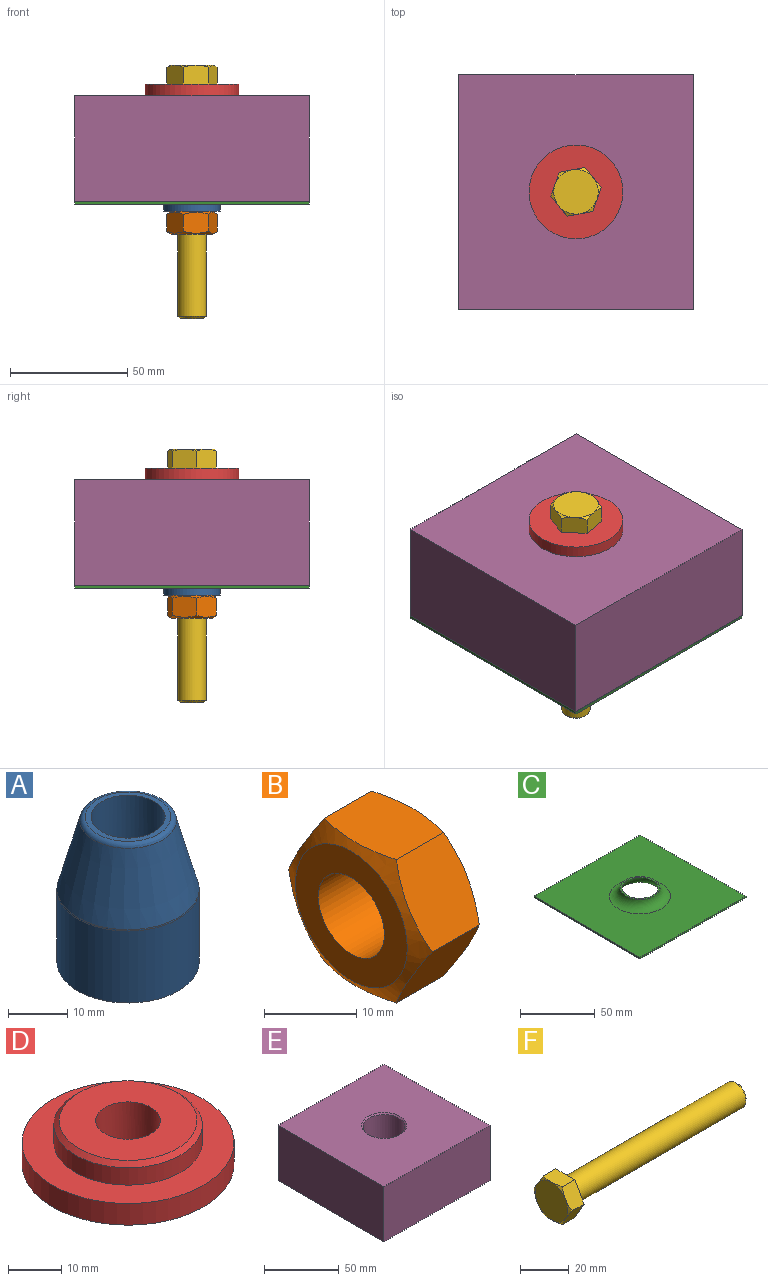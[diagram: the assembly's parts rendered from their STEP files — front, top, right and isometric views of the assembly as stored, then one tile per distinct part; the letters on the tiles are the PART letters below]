
ASSEMBLY  parts=6 mates=10
PART A: 7 faces, bbox 26x26x30 mm
  f0: cylinder r=12mm len=24mm, axis (0,0,-1), area 1121mm2, adj f2,f5
  f1: plane 14.43x14.43mm, normal (0,0,1), area 40.8mm2, adj f3,f6
  f2: plane 24x24mm, normal (0,0,-1), area 329.7mm2, adj f0,f3
  f3: cylinder r=6.25mm len=30mm, axis (0,0,-1), area 1178.1mm2, adj f1,f2
  f4: cone r=7.98mm half-angle=15deg, axis (0,0,-1), area 925.9mm2, adj f5,f6
  f5: torus R=11mm, axis (0,0,1), area 19.7mm2, adj f0,f4
  f6: torus R=7.21mm, axis (0,0,1), area 64mm2, adj f1,f4
PART B: 11 faces, bbox 10x21.9x21.9 mm
  f0: plane 17.1x17.1mm, normal (1,0,0), area 149.4mm2, adj f1,f4
  f1: cone r=11.4mm half-angle=60deg, axis (-1,0,0), area 95.8mm2, adj f0,f5,f6,f7,f8,f9,f10
  f2: cone r=8.55mm half-angle=60deg, axis (1,0,0), area 95.8mm2, adj f3,f5,f6,f7,f8,f9,f10
  f3: plane 17.1x17.1mm, normal (-1,0,0), area 149.4mm2, adj f2,f4
  f4: cylinder r=5.05mm len=10.11mm, axis (1,0,0), area 317.5mm2, adj f0,f3
  f5: plane 10.98x8.91mm, normal (0,0,1), area 91.3mm2, adj f1,f2,f6,f10
  f6: plane 9.5x8.91mm, normal (0,0.87,0.5), area 91.3mm2, adj f1,f2,f5,f7
  f7: plane 9.5x8.91mm, normal (0,0.87,-0.5), area 91.3mm2, adj f1,f2,f6,f8
  f8: plane 10.98x8.91mm, normal (0,0,-1), area 91.3mm2, adj f1,f2,f7,f9
  f9: plane 9.5x8.91mm, normal (0,-0.87,-0.5), area 91.3mm2, adj f1,f2,f8,f10
  f10: plane 9.5x8.91mm, normal (0,-0.87,0.5), area 91.3mm2, adj f1,f2,f5,f9
PART C: 9 faces, bbox 100x100x8.4 mm
  f0: plane 100x1.2mm, normal (0,-1,0), area 120mm2, adj f1,f3,f5,f7
  f1: plane 100x1.2mm, normal (-1,0,0), area 120mm2, adj f0,f2,f5,f7
  f2: plane 100x1.2mm, normal (0,1,0), area 120mm2, adj f1,f3,f5,f7
  f3: plane 100x1.2mm, normal (1,0,0), area 120mm2, adj f0,f2,f5,f7
  f4: plane 26.4x26.4mm, normal (0,0,1), area 95.1mm2, adj f6,f8
  f5: plane 100x100mm, normal (0,0,-1), area 8693.8mm2, adj f0,f1,f2,f3,f6
  f6: torus R=20.39mm, axis (0,0,1), area 1217mm2, adj f4,f5
  f7: plane 100x100mm, normal (0,0,1), area 8693.8mm2, adj f0,f1,f2,f3,f8
  f8: torus R=20.39mm, axis (0,0,1), area 1090.1mm2, adj f4,f7
PART D: 7 faces, bbox 40x40x10 mm
  f0: cylinder r=20mm len=40mm, axis (0,0,-1), area 628.3mm2, adj f1,f2
  f1: plane 40x40mm, normal (0,0,1), area 640.9mm2, adj f0,f3
  f2: plane 40x40mm, normal (0,0,-1), area 1139.7mm2, adj f0,f5
  f3: cylinder r=14mm len=28mm, axis (0,0,-1), area 351.9mm2, adj f1,f6
  f4: plane 26x26mm, normal (0,0,1), area 414mm2, adj f5,f6
  f5: cylinder r=6.1mm len=12.2mm, axis (0,0,-1), area 383.3mm2, adj f2,f4
  f6: cone r=13mm half-angle=45deg, axis (0,0,-1), area 120mm2, adj f3,f4
PART E: 9 faces, bbox 100x100x45 mm
  f0: plane 100x45mm, normal (1,0,0), area 4500mm2, adj f1,f3,f4,f5
  f1: plane 100x45mm, normal (0,1,0), area 4500mm2, adj f0,f2,f4,f5
  f2: plane 100x45mm, normal (-1,0,0), area 4500mm2, adj f1,f3,f4,f5
  f3: plane 100x45mm, normal (0,-1,0), area 4500mm2, adj f0,f2,f4,f5
  f4: plane 100x100mm, normal (0,0,1), area 9293.1mm2, adj f0,f1,f2,f3,f8
  f5: plane 100x100mm, normal (0,0,-1), area 8743.4mm2, adj f0,f1,f2,f3,f7
  f6: cylinder r=14mm len=38mm, axis (0,0,-1), area 3342.7mm2, adj f7,f8
  f7: torus R=20mm, axis (0,0,1), area 958.2mm2, adj f5,f6
  f8: cone r=15mm half-angle=45deg, axis (0,0,1), area 128.8mm2, adj f4,f6
PART F: 18 faces, bbox 108x21.9x21.9 mm
  f0: plane 21.94x19mm, normal (1,0,0), area 158.7mm2, adj f1,f5,f6,f7,f8,f9,f10
  f1: torus R=7mm, axis (1,0,0), area 62.8mm2, adj f0,f4
  f2: plane 9.85x9.85mm, normal (1,0,0), area 76.2mm2, adj f3
  f3: cone r=6mm half-angle=45deg, axis (-1,0,0), area 52.1mm2, adj f2,f4
  f4: cylinder r=6mm len=97.93mm, axis (1,0,0), area 3691.7mm2, adj f1,f3
  f5: plane 10.98x8mm, normal (0,0,1), area 84.6mm2, adj f0,f6,f10,f11,f12
  f6: plane 9.5x8mm, normal (0,0.87,0.5), area 84.6mm2, adj f0,f5,f7,f11,f15
  f7: plane 9.5x8mm, normal (0,0.87,-0.5), area 84.6mm2, adj f0,f6,f8,f14,f15
  f8: plane 10.98x8mm, normal (0,0,-1), area 84.6mm2, adj f0,f7,f9,f13,f14
  f9: plane 9.5x8mm, normal (0,-0.87,-0.5), area 84.6mm2, adj f0,f8,f10,f13,f17
  f10: plane 9.5x8mm, normal (0,-0.87,0.5), area 84.6mm2, adj f0,f5,f9,f12,f17
  f11: cone r=9.5mm half-angle=60deg, axis (1,0,0), area 5.6mm2, adj f5,f6,f16
  f12: cone r=9.5mm half-angle=60deg, axis (1,0,0), area 5.6mm2, adj f5,f10,f16
  f13: cone r=9.5mm half-angle=60deg, axis (1,0,0), area 5.6mm2, adj f8,f9,f16
  f14: cone r=9.5mm half-angle=60deg, axis (1,0,0), area 5.6mm2, adj f7,f8,f16
  f15: cone r=9.5mm half-angle=60deg, axis (1,0,0), area 5.6mm2, adj f6,f7,f16
  f16: plane 19x19mm, normal (-1,0,0), area 283.5mm2, adj f11,f12,f13,f14,f15,f17
  f17: cone r=9.5mm half-angle=60deg, axis (1,0,0), area 5.6mm2, adj f9,f10,f16
PLACE A rot(axis=(0,0,-1),169.6deg) t=(0,0,-48.1)mm
PLACE B rot(axis=(-0.54,-0.65,-0.54),114.2deg) t=(0,0,-58.1)mm
PLACE C rot(axis=(0,0,-1),0deg) t=(0,0,-45.2)mm
PLACE D rot(axis=(0.05,-1,0),180deg) t=(0,0,6)mm
PLACE E rot(axis=(0,0,-1),90deg) t=(0,0,-44)mm fixed
PLACE F rot(axis=(0.54,0.65,-0.54),114.2deg) t=(0,0,6)mm
MATE cylindrical E.f6 <-> A.f0  axis (0,0,-1) through (0,0,-19)mm
MATE planar C.f6 <-> E.f6  axis (0,0,1) through (0,0,-44)mm
MATE cylindrical E.f6 <-> D.f0  axis (0,0,1) through (0,0,1)mm
MATE planar B.f1 <-> A.f0  axis (0,0,1) through (0,0,-48.1)mm
MATE planar E.f0 <-> C.f0  axis (0,-1,0) through (0,-50,-21.5)mm
MATE planar F.f0 <-> D.f0  axis (0,0,-1) through (-1.71,9.34,6)mm
MATE cylindrical C.f6 <-> E.f6  axis (0,0,1) through (0,0,-44)mm
MATE planar D.f0 <-> E.f6  axis (0,0,-1) through (0,0,1)mm
MATE cylindrical F.f3 <-> D.f0  axis (0,0,-1) through (0,0,5)mm
MATE slider B.f1 <-> F.f3  axis (0,0,1) through (0,0,-48.1)mm
